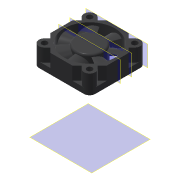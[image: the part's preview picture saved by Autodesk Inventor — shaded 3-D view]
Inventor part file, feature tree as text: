
AUTODESK INVENTOR PART (.ipt)
format: ipt  version: 2016 (Build 200138000, 138)  size: 386,048 bytes
history: native  units: mm
features: sketch x8, extrude x6, plane x3, fillet x2, pattern_circular x2, loft x1, projected_geometry x1
ambient origin geometry x8: Origin, YZ Plane, XZ Plane, XY Plane, X Axis, Y Axis, Z Axis, Center Point
bodies: Solid1 (feature_tree), Solid2 (feature_tree)
feature tree (23):
  extrude  "Extrusion1"  Depth=10.0mm
  plane  "Work Plane1"
  fillet  "Fillet1"  Radius=10.0mm
  extrude  "Extrusion3"  Depth=3.0mm
  extrude  "Extrusion4"  Depth=3.0mm
  extrude  "Extrusion5"  Depth=100.0mm TaperAngle=0.0deg
  pattern_circular  "Circular Pattern1"  Count=3 Angle=360.0deg
  fillet  "Fillet2"  Radius=1.0mm
  plane  "Work Plane2"
  sketch  "Sketch6"  dims[d13=15.0mm]
  plane  "Work Plane3"
  loft  "Loft1"
  extrude  "Extrusion6"  TaperAngle=0.0deg  [1 undecoded]
  pattern_circular  "Circular Pattern2"  [2 undecoded]
  extrude  "Extrusion7"  Depth=10.0mm TaperAngle=360.0deg
  sketch  "Sketch1"  dims[d0=30.0mm d1=30.0mm d2=10.0mm d3=0.0mm]
  sketch  "Sketch3"  dims[d6=3.0mm d7=3.0mm]
  sketch  "Sketch4"  dims[d8=3.0mm d9=3.0mm]
  sketch  "Sketch5"  dims[d10=3.0mm d11=100.0mm d12=0.0mm]
  sketch  "Sketch7"  dims[d14=10.0mm d15=0.0mm]
  sketch  "Sketch8"  dims[d16=1.0mm d17=0.0mm d18=30.0mm d19=360.0deg d21=1.0mm]
  sketch  "Sketch9"  dims[d22=6.0mm d23=8.5mm d24=0.0mm d25=90.0deg d26=0.0mm d27=90.0deg d28=10.0mm d29=0.0mm d30=70.0mm d31=360.0deg d33=29.5mm d34=29.5mm d35=7.0mm d36=0.0mm]
  projected_geometry  "Projected Loop1"
note: 3 required parameter values undecoded (feature->parameter linkage not recoverable at this tier; creation-order binding heuristic only, values carry confidence <= 0.55)
